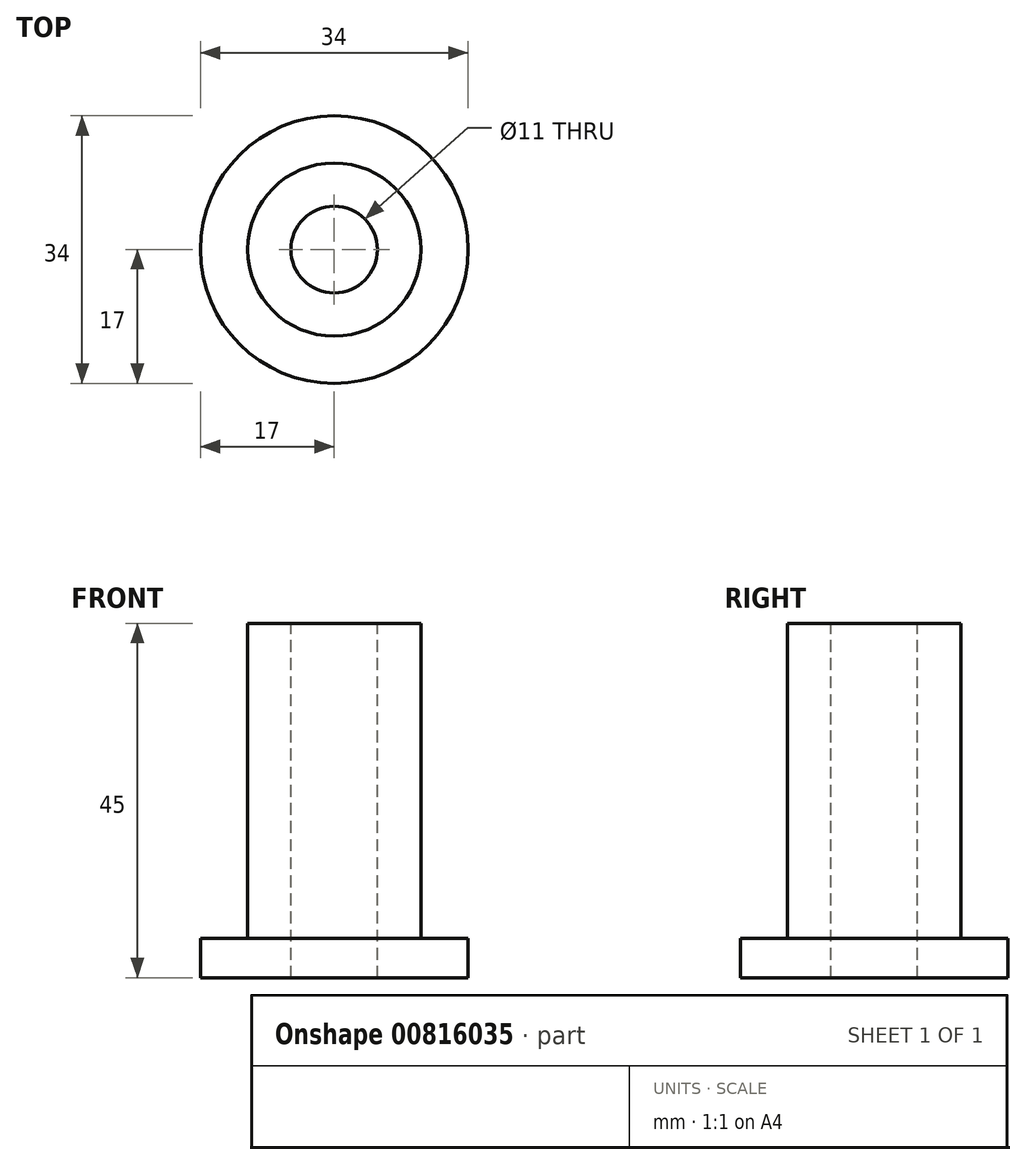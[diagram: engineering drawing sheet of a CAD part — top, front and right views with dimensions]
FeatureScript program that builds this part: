
annotation { "Feature Type Name" : "Feature", "Feature Type Description" : "" }
export const myFeature = defineFeature(function(context is Context, id is Id, definition is map)
    precondition{}
    {
        {
            var Q0;
            Q0=qCreatedBy(makeId("Front.planeOp"),FACE);
            var sketch = newSketch(context, id + "F0", { "sketchPlane" : qUnion([Q0])});
            skLineSegment(sketch, "E0", {"start": v(0, 0) * mm, "end": v(-17, 0) * mm});
            skLineSegment(sketch, "E1", {"start": v(-17, 0) * mm, "end": v(-17, 5) * mm});
            skLineSegment(sketch, "E2", {"start": v(0, 0) * mm, "end": v(0, 45) * mm});
            skLineSegment(sketch, "E3", {"start": v(0, 45) * mm, "end": v(-11, 45) * mm});
            skLineSegment(sketch, "E4", {"start": v(-11, 45) * mm, "end": v(-11, 5) * mm});
            skLineSegment(sketch, "E5", {"start": v(-11, 5) * mm, "end": v(-17, 5) * mm});
            skLineSegment(sketch, "E6", {"start": v(0, 45) * mm, "end": v(5, 45) * mm, "construction": true});
            skSolve(sketch);
        }
        {
            var Q0;
            Q0 = qSketchRegion(id + "F0", true);
            var Q1;
            Q1=sQuery(id+"F0.wireOp",EDGE,"E2");
            revolve(context, id + "F1", {"surfaceOperationType" : NewSurfaceOperationType.NEW, "entities" : qUnion([Q0]), "axis" : qUnion([Q1]), "revolveType" : RevolveType.FULL});
        }
        {
            var Q0;
            Q0=makeQuery(id+"F1.opRevolve","SWEPT_FACE",FACE,{"disambiguationData":[OSD([sQuery(id+"F0.wireOp",EDGE,"E3")])]});
            var sketch = newSketch(context, id + "F2", { "sketchPlane" : qUnion([Q0])});
            skPoint(sketch, "E7", {"position": v(0, 0) * mm});
            skSolve(sketch);
        }
        {
            var Q0;
            Q0=sQuery(id+"F2.wireOp",VERTEX,"E7");
            var Q1;
            Q1=makeQuery(id+"F1.opRevolve","SWEPT_BODY",BODY,{"disambiguationData":[OSD([sQuery(id+"F0.wireOp",EDGE,"E0"),sQuery(id+"F0.wireOp",EDGE,"E1"),sQuery(id+"F0.wireOp",EDGE,"E2"),sQuery(id+"F0.wireOp",EDGE,"E3"),sQuery(id+"F0.wireOp",EDGE,"E4"),sQuery(id+"F0.wireOp",EDGE,"E5")])]});
            hole(context, id + "F3", {"style" : HoleStyle.SIMPLE, "endStyle" : HoleEndStyle.BLIND, "standardTappedOrClearance" : lookupTablePath({ "standard" : "ISO", "fit" : "Normal", "size" : "M10", "type" : "Clearance" }), "standardBlindInLast" : lookupTablePath({ "fit" : "Standard", "standard" : "ISO", "size" : "M10", "type" : "Clearance" }), "holeDiameter" : 11 * mm, "majorDiameter" : 5 * mm, "holeDepth" : 45 * mm, "isTappedThrough" : true, "tappedDepth" : 12 * mm, "tapClearance" : 3, "startFromSketch" : true, "locations" : qUnion([Q0]), "scope" : qUnion([Q1])});
        }
    });
